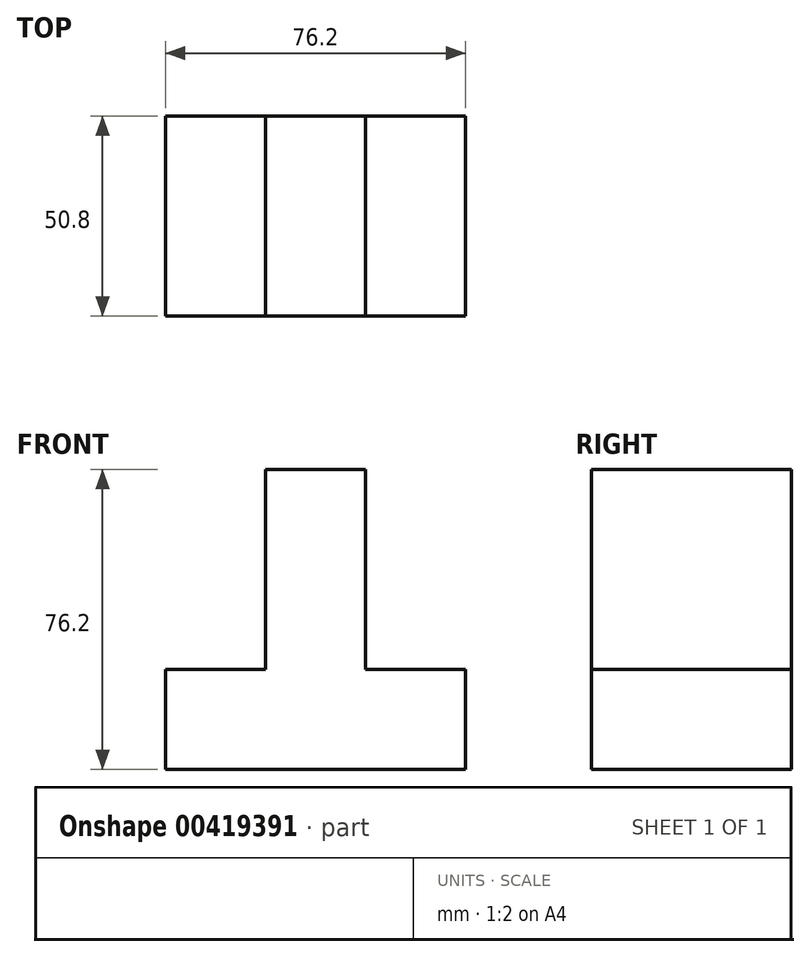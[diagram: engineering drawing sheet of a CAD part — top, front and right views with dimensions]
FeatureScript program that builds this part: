
annotation { "Feature Type Name" : "Feature", "Feature Type Description" : "" }
export const myFeature = defineFeature(function(context is Context, id is Id, definition is map)
    precondition{}
    {
        {
            var Q0;
            Q0=qCreatedBy(makeId("Front.planeOp"),FACE);
            var sketch = newSketch(context, id + "F0", { "sketchPlane" : qUnion([Q0])});
            skLineSegment(sketch, "E0", {"start": v(-51.37, -29.79) * mm, "end": v(24.83, -29.79) * mm});
            skLineSegment(sketch, "E1", {"start": v(24.83, -29.79) * mm, "end": v(24.83, -4.39) * mm});
            skLineSegment(sketch, "E2", {"start": v(24.83, -4.39) * mm, "end": v(-0.57, -4.39) * mm});
            skLineSegment(sketch, "E3", {"start": v(-0.57, -4.39) * mm, "end": v(-0.57, 46.41) * mm});
            skLineSegment(sketch, "E4", {"start": v(-0.57, 46.41) * mm, "end": v(-25.97, 46.41) * mm});
            skLineSegment(sketch, "E5", {"start": v(-25.97, 46.41) * mm, "end": v(-25.97, -4.39) * mm});
            skLineSegment(sketch, "E6", {"start": v(-25.97, -4.39) * mm, "end": v(-51.37, -4.39) * mm});
            skLineSegment(sketch, "E7", {"start": v(-51.37, -4.39) * mm, "end": v(-51.37, -29.79) * mm});
            skSolve(sketch);
        }
        {
            var Q0;
            Q0 = qSketchRegion(id + "F0", true);
            extrude(context, id + "F1", {"entities" : qUnion([Q0]), "depth" : 50.8 * mm});
        }
    });
